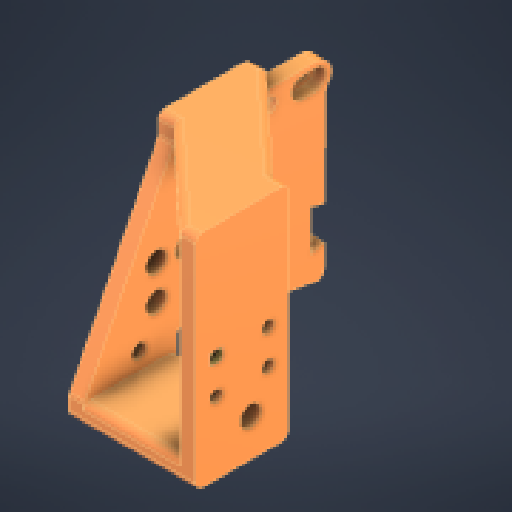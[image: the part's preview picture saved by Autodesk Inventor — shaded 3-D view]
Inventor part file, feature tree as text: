
AUTODESK INVENTOR PART (.ipt)
format: ipt  version: 2025 (Build 290162000, 162)  size: 399,360 bytes
history: native  units: mm
features: extrude x10, sketch x10, reference x5, other x4, projected_geometry x2, plane x1, fillet x1
ambient origin geometry x8: Origin, YZ Plane, XZ Plane, XY Plane, X Axis, Y Axis, Z Axis, Center Point
bodies: Solid1 (feature_tree)
feature tree (33):
  plane  "Work Plane1"
  extrude  "Extrusion1"  Depth=6.0mm
  extrude  "Extrusion2"  Depth=6.0mm
  extrude  "Extrusion3"  Depth=3.5mm
  extrude  "Extrusion4"  Depth=3.5mm
  extrude  "Extrusion5"  Depth=6.0mm
  extrude  "Extrusion6"  Depth=6.0mm
  extrude  "Extrusion7"  Depth=6.0mm TaperAngle=0.0deg
  extrude  "Extrusion8"  Depth=10.0mm TaperAngle=0.0deg
  extrude  "Extrusion9"  Depth=6.0mm TaperAngle=0.0deg
  extrude  "Extrusion10"  Depth=10.0mm TaperAngle=0.0deg
  fillet  "Fillet1"  Radius=27.0mm
  sketch  "Sketch1"  dims[d0=6.0mm d1=6.0mm]
  reference  "Reference1"
  reference  "Reference2"
  reference  "Reference3"
  reference  "Reference4"
  sketch  "Sketch2"  dims[d2=6.0mm d3=6.0mm]
  sketch  "Sketch3"  dims[d4=3.5mm d5=3.5mm]
  projected_geometry  "Projected Loop1"
  sketch  "Sketch4"  dims[d6=3.5mm d7=3.5mm]
  sketch  "Sketch5"  dims[d8=4.5mm d9=0.0mm d10=6.0mm]
  sketch  "Sketch6"  dims[d11=6.0mm d12=6.0mm]
  projected_geometry  "Projected Loop2"
  sketch  "Sketch7"  dims[d13=6.0mm d14=3.0mm d15=0.0mm]
  sketch  "Sketch8"  dims[d16=3.0mm d17=0.0mm d18=10.0mm d19=0.0mm]
  sketch  "Sketch9"  dims[d20=27.0mm d21=6.0mm d22=0.0mm]
  reference  "Reference5"
  sketch  "Sketch10"  dims[d23=4.999996mm d24=10.0mm d25=0.0mm d26=27.0mm d27=6.0mm d28=0.0mm d29=6.0mm d30=0.0mm d31=6.0mm d32=10.0mm d33=0.0mm d34=6.0mm d35=0.0mm d37=2.0mm]
  other  "Part 2"
  other  "hotend-new.iam"
  other  "bolts reference:1"
  other  "Radial_Fan_50x15 v8:1"
